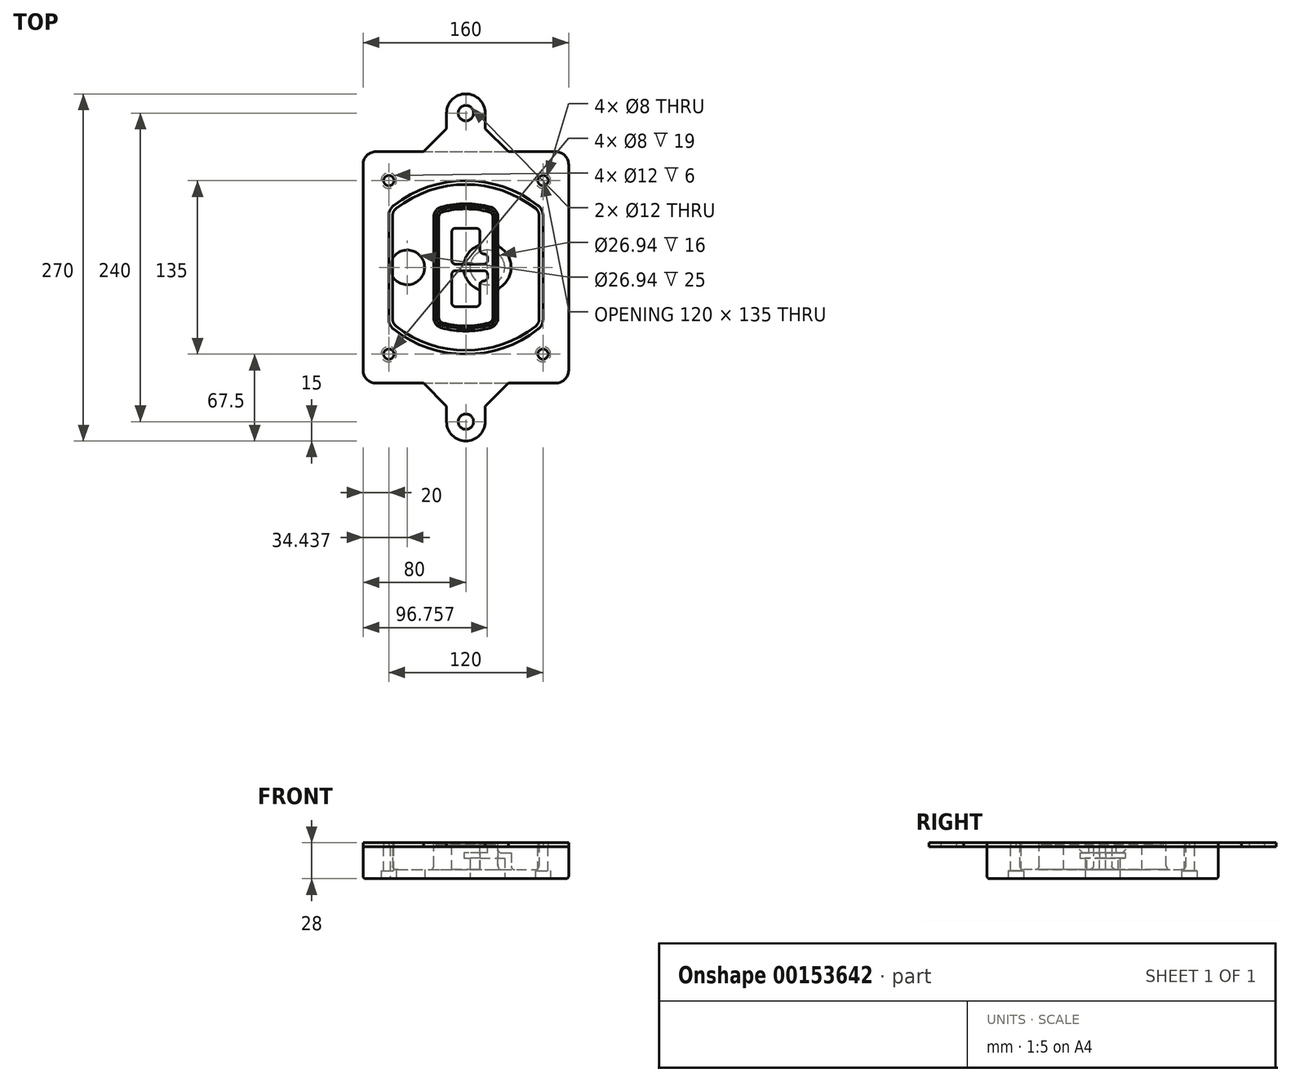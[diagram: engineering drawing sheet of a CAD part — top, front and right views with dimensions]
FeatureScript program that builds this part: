
annotation { "Feature Type Name" : "Feature", "Feature Type Description" : "" }
export const myFeature = defineFeature(function(context is Context, id is Id, definition is map)
    precondition{}
    {
        {
            var Q0;
            Q0=qCreatedBy(makeId("Top.planeOp"),FACE);
            var sketch = newSketch(context, id + "F0", { "sketchPlane" : qUnion([Q0])});
            skPoint(sketch, "E0.rect.middle", {"position": v(0, 0) * mm});
            skLineSegment(sketch, "E1.bottom", {"start": v(-70, -90) * mm, "end": v(70, -90) * mm});
            skLineSegment(sketch, "E1.top", {"start": v(-70, 90) * mm, "end": v(70, 90) * mm});
            skLineSegment(sketch, "E1.left", {"start": v(-80, -80) * mm, "end": v(-80, 80) * mm});
            skLineSegment(sketch, "E1.right", {"start": v(80, -80) * mm, "end": v(80, 80) * mm});
            skLineSegment(sketch, "E2", {"start": v(-80, 90) * mm, "end": v(80, -90) * mm, "construction": true});
            skLineSegment(sketch, "E3", {"start": v(80, 90) * mm, "end": v(-80, -90) * mm, "construction": true});
            skCircle(sketch, "E4", {"center": v(-60, 67.5) * mm, "radius": 4 * mm});
            skCircle(sketch, "E5", {"center": v(60, 67.5) * mm, "radius": 4 * mm});
            skCircle(sketch, "E6", {"center": v(60, -67.5) * mm, "radius": 4 * mm});
            skCircle(sketch, "E7", {"center": v(-60, -67.5) * mm, "radius": 4 * mm});
            skLineSegment(sketch, "E8", {"start": v(-60, 67.5) * mm, "end": v(60, 67.5) * mm, "construction": true});
            skLineSegment(sketch, "E9", {"start": v(60, 67.5) * mm, "end": v(60, -67.5) * mm, "construction": true});
            skLineSegment(sketch, "E10", {"start": v(60, -67.5) * mm, "end": v(-60, -67.5) * mm, "construction": true});
            skLineSegment(sketch, "E11", {"start": v(-60, -67.5) * mm, "end": v(-60, 67.5) * mm, "construction": true});
            skLineSegment(sketch, "E12", {"start": v(-60, 40.3) * mm, "end": v(-60, -40.3) * mm});
            skLineSegment(sketch, "E13", {"start": v(60, 40.3) * mm, "end": v(60, -40.3) * mm});
            skArc(sketch, "E14", {"start": v(56.15, 48.18) * mm, "mid": v(0, 67.5) * mm, "end": v(-56.15, 48.18) * mm});
            skArc(sketch, "E15", {"start": v(-56.15, -48.18) * mm, "mid": v(0, -67.5) * mm, "end": v(56.15, -48.18) * mm});
            skLineSegment(sketch, "E16", {"start": v(-60, 0) * mm, "end": v(60, 0) * mm, "construction": true});
            skPoint(sketch, "E17.visualSharp", {"position": v(-60, -45) * mm});
            skArc(sketch, "E17.filletArc", {"start": v(-60, -40.3) * mm, "mid": v(-58.99, -44.68) * mm, "end": v(-56.15, -48.18) * mm});
            skPoint(sketch, "E18.visualSharp", {"position": v(-60, 45) * mm});
            skArc(sketch, "E18.filletArc", {"start": v(-56.15, 48.18) * mm, "mid": v(-58.99, 44.68) * mm, "end": v(-60, 40.3) * mm});
            skPoint(sketch, "E19.visualSharp", {"position": v(60, 45) * mm});
            skArc(sketch, "E19.filletArc", {"start": v(60, 40.3) * mm, "mid": v(58.99, 44.68) * mm, "end": v(56.15, 48.18) * mm});
            skPoint(sketch, "E20.visualSharp", {"position": v(60, -45) * mm});
            skArc(sketch, "E20.filletArc", {"start": v(56.15, -48.18) * mm, "mid": v(58.99, -44.68) * mm, "end": v(60, -40.3) * mm});
            skPoint(sketch, "E21.visualSharp", {"position": v(-80, 90) * mm});
            skArc(sketch, "E21.filletArc", {"start": v(-70, 90) * mm, "mid": v(-77.07, 87.07) * mm, "end": v(-80, 80) * mm});
            skPoint(sketch, "E22.visualSharp", {"position": v(80, 90) * mm});
            skArc(sketch, "E22.filletArc", {"start": v(80, 80) * mm, "mid": v(77.07, 87.07) * mm, "end": v(70, 90) * mm});
            skPoint(sketch, "E23.visualSharp", {"position": v(80, -90) * mm});
            skArc(sketch, "E23.filletArc", {"start": v(70, -90) * mm, "mid": v(77.07, -87.07) * mm, "end": v(80, -80) * mm});
            skPoint(sketch, "E24.visualSharp", {"position": v(-80, -90) * mm});
            skArc(sketch, "E24.filletArc", {"start": v(-80, -80) * mm, "mid": v(-77.07, -87.07) * mm, "end": v(-70, -90) * mm});
            skArc(sketch, "E25.0", {"start": v(57, 40.3) * mm, "mid": v(56.3, 43.36) * mm, "end": v(54.3, 45.81) * mm});
            skLineSegment(sketch, "E25.1", {"start": v(57, 40.3) * mm, "end": v(57, -40.3) * mm});
            skArc(sketch, "E25.2", {"start": v(54.3, -45.81) * mm, "mid": v(56.3, -43.36) * mm, "end": v(57, -40.3) * mm});
            skArc(sketch, "E25.3", {"start": v(-54.3, -45.81) * mm, "mid": v(0, -64.5) * mm, "end": v(54.3, -45.81) * mm});
            skArc(sketch, "E25.4", {"start": v(-57, -40.3) * mm, "mid": v(-56.3, -43.36) * mm, "end": v(-54.3, -45.81) * mm});
            skArc(sketch, "E25.5", {"start": v(54.3, 45.81) * mm, "mid": v(0, 64.5) * mm, "end": v(-54.3, 45.81) * mm});
            skLineSegment(sketch, "E25.6", {"start": v(-57, 40.3) * mm, "end": v(-57, -40.3) * mm});
            skArc(sketch, "E25.7", {"start": v(-54.3, 45.81) * mm, "mid": v(-56.3, 43.36) * mm, "end": v(-57, 40.3) * mm});
            skArc(sketch, "E26.0", {"start": v(-58.62, 51.33) * mm, "mid": v(-62.58, 46.43) * mm, "end": v(-64, 40.3) * mm});
            skArc(sketch, "E26.1", {"start": v(58.62, 51.33) * mm, "mid": v(0, 71.5) * mm, "end": v(-58.62, 51.33) * mm});
            skArc(sketch, "E26.2", {"start": v(64, 40.3) * mm, "mid": v(62.58, 46.43) * mm, "end": v(58.62, 51.33) * mm});
            skLineSegment(sketch, "E26.3", {"start": v(64, 40.3) * mm, "end": v(64, -40.3) * mm});
            skArc(sketch, "E26.4", {"start": v(58.62, -51.33) * mm, "mid": v(62.58, -46.43) * mm, "end": v(64, -40.3) * mm});
            skLineSegment(sketch, "E26.5", {"start": v(-64, 40.3) * mm, "end": v(-64, -40.3) * mm});
            skArc(sketch, "E26.6", {"start": v(-58.62, -51.33) * mm, "mid": v(0, -71.5) * mm, "end": v(58.62, -51.33) * mm});
            skArc(sketch, "E26.7", {"start": v(-64, -40.3) * mm, "mid": v(-62.58, -46.43) * mm, "end": v(-58.62, -51.33) * mm});
            skSolve(sketch);
        }
        {
            var Q0;
            Q0=makeQuery(id+"F0.imprint","IMPRINT",FACE,{"disambiguationData":[TD([[makeQuery(id+"F0.imprint","IMPRINT",EDGE,{"derivedFrom":sQuery(id+"F0.wireOp",EDGE,"E1.bottom")}),1.0]])]});
            var Q1;
            Q1=makeQuery(id+"F0.imprint","IMPRINT",FACE,{"disambiguationData":[TD([[makeQuery(id+"F0.imprint","IMPRINT",EDGE,{"derivedFrom":sQuery(id+"F0.wireOp",EDGE,"E12")}),1.0]])]});
            var Q2;
            Q2=makeQuery(id+"F0.imprint","IMPRINT",FACE,{"disambiguationData":[TD([[makeQuery(id+"F0.imprint","IMPRINT",EDGE,{"derivedFrom":sQuery(id+"F0.wireOp",EDGE,"E25.0")}),1.0]])]});
            var Q3;
            Q3=makeQuery(id+"F0.imprint","IMPRINT",FACE,{"disambiguationData":[TD([[makeQuery(id+"F0.imprint","IMPRINT",EDGE,{"derivedFrom":sQuery(id+"F0.wireOp",EDGE,"E12")}),-1.0]])]});
            extrude(context, id + "F1", {"entities" : qUnion([Q0, Q1, Q2, Q3]), "oppositeDirection" : true, "depth" : 25 * mm});
        }
        {
            var Q0;
            Q0=makeQuery(id+"F0.imprint","IMPRINT",FACE,{"disambiguationData":[TD([[makeQuery(id+"F0.imprint","IMPRINT",EDGE,{"derivedFrom":sQuery(id+"F0.wireOp",EDGE,"E12")}),1.0]])]});
            extrude(context, id + "F2", {"entities" : qUnion([Q0]), "operationType" : NewBodyOperationType.ADD, "depth" : 3 * mm});
        }
        {
            var Q0;
            Q0=makeQuery(id+"F0.imprint","IMPRINT",FACE,{"disambiguationData":[TD([[makeQuery(id+"F0.imprint","IMPRINT",EDGE,{"derivedFrom":sQuery(id+"F0.wireOp",EDGE,"E25.0")}),1.0]])]});
            extrude(context, id + "F3", {"entities" : qUnion([Q0]), "operationType" : NewBodyOperationType.REMOVE, "oppositeDirection" : true, "depth" : 18 * mm});
        }
        {
            var Q0;
            Q0=makeQuery(id+"F2.opExtrude","CAP_FACE",FACE,{"disambiguationData":[OSD([sQuery(id+"F0.wireOp",EDGE,"E12"),sQuery(id+"F0.wireOp",EDGE,"E13"),sQuery(id+"F0.wireOp",EDGE,"E14"),sQuery(id+"F0.wireOp",EDGE,"E15"),sQuery(id+"F0.wireOp",EDGE,"E17.filletArc"),sQuery(id+"F0.wireOp",EDGE,"E18.filletArc"),sQuery(id+"F0.wireOp",EDGE,"E19.filletArc"),sQuery(id+"F0.wireOp",EDGE,"E20.filletArc"),sQuery(id+"F0.wireOp",EDGE,"E25.0"),sQuery(id+"F0.wireOp",EDGE,"E25.1"),sQuery(id+"F0.wireOp",EDGE,"E25.2"),sQuery(id+"F0.wireOp",EDGE,"E25.3"),sQuery(id+"F0.wireOp",EDGE,"E25.4"),sQuery(id+"F0.wireOp",EDGE,"E25.5"),sQuery(id+"F0.wireOp",EDGE,"E25.6"),sQuery(id+"F0.wireOp",EDGE,"E25.7")])],"isStart":false});
            var sketch = newSketch(context, id + "F4", { "sketchPlane" : qUnion([Q0])});
            skArc(sketch, "E27.0", {"start": v(-19.08, -46.97) * mm, "mid": v(0, -49.5) * mm, "end": v(19.08, -46.97) * mm});
            skArc(sketch, "E28.0", {"start": v(19.08, 46.97) * mm, "mid": v(0, 49.5) * mm, "end": v(-19.08, 46.97) * mm});
            skLineSegment(sketch, "E29", {"start": v(-25, 39.25) * mm, "end": v(-25, -39.25) * mm});
            skLineSegment(sketch, "E30", {"start": v(25, 39.25) * mm, "end": v(25, -39.25) * mm});
            skLineSegment(sketch, "E31", {"start": v(-25, 45.1) * mm, "end": v(25, 45.1) * mm, "construction": true});
            skLineSegment(sketch, "E32", {"start": v(-25, -45.1) * mm, "end": v(25, -45.1) * mm, "construction": true});
            skPoint(sketch, "E33.visualSharp", {"position": v(-25, 45.1) * mm});
            skArc(sketch, "E33.filletArc", {"start": v(-19.08, 46.97) * mm, "mid": v(-23.35, 44.11) * mm, "end": v(-25, 39.25) * mm});
            skPoint(sketch, "E34.visualSharp", {"position": v(25, 45.1) * mm});
            skArc(sketch, "E34.filletArc", {"start": v(25, 39.25) * mm, "mid": v(23.35, 44.11) * mm, "end": v(19.08, 46.97) * mm});
            skPoint(sketch, "E35.visualSharp", {"position": v(25, -45.1) * mm});
            skArc(sketch, "E35.filletArc", {"start": v(19.08, -46.97) * mm, "mid": v(23.35, -44.11) * mm, "end": v(25, -39.25) * mm});
            skPoint(sketch, "E36.visualSharp", {"position": v(-25, -45.1) * mm});
            skArc(sketch, "E36.filletArc", {"start": v(-25, -39.25) * mm, "mid": v(-23.35, -44.11) * mm, "end": v(-19.08, -46.97) * mm});
            skArc(sketch, "E37.0", {"start": v(54.3, 45.81) * mm, "mid": v(0, 64.5) * mm, "end": v(-54.3, 45.81) * mm});
            skArc(sketch, "E37.1", {"start": v(-54.3, 45.81) * mm, "mid": v(-56.3, 43.36) * mm, "end": v(-57, 40.3) * mm});
            skLineSegment(sketch, "E37.2", {"start": v(-57, 40.3) * mm, "end": v(-57, -40.3) * mm});
            skArc(sketch, "E37.3", {"start": v(-57, -40.3) * mm, "mid": v(-56.3, -43.36) * mm, "end": v(-54.3, -45.81) * mm});
            skArc(sketch, "E37.4", {"start": v(-54.3, -45.81) * mm, "mid": v(0, -64.5) * mm, "end": v(54.3, -45.81) * mm});
            skArc(sketch, "E37.5", {"start": v(54.3, -45.81) * mm, "mid": v(56.3, -43.36) * mm, "end": v(57, -40.3) * mm});
            skLineSegment(sketch, "E37.6", {"start": v(57, 40.3) * mm, "end": v(57, -40.3) * mm});
            skArc(sketch, "E37.7", {"start": v(57, 40.3) * mm, "mid": v(56.3, 43.36) * mm, "end": v(54.3, 45.81) * mm});
            skLineSegment(sketch, "E38.0", {"start": v(23, 39.25) * mm, "end": v(23, -39.25) * mm});
            skArc(sketch, "E38.1", {"start": v(18.56, -45.04) * mm, "mid": v(21.76, -42.9) * mm, "end": v(23, -39.25) * mm});
            skArc(sketch, "E38.2", {"start": v(-18.56, -45.04) * mm, "mid": v(0, -47.5) * mm, "end": v(18.56, -45.04) * mm});
            skArc(sketch, "E38.3", {"start": v(-23, -39.25) * mm, "mid": v(-21.76, -42.9) * mm, "end": v(-18.56, -45.04) * mm});
            skLineSegment(sketch, "E38.4", {"start": v(-23, 39.25) * mm, "end": v(-23, -39.25) * mm});
            skArc(sketch, "E38.5", {"start": v(23, 39.25) * mm, "mid": v(21.76, 42.9) * mm, "end": v(18.56, 45.04) * mm});
            skArc(sketch, "E38.6", {"start": v(-18.56, 45.04) * mm, "mid": v(-21.76, 42.9) * mm, "end": v(-23, 39.25) * mm});
            skArc(sketch, "E38.7", {"start": v(18.56, 45.04) * mm, "mid": v(0, 47.5) * mm, "end": v(-18.56, 45.04) * mm});
            skArc(sketch, "E39.0", {"start": v(21, 39.25) * mm, "mid": v(20.18, 41.68) * mm, "end": v(18.04, 43.1) * mm});
            skLineSegment(sketch, "E39.1", {"start": v(21, 39.25) * mm, "end": v(21, -39.25) * mm});
            skArc(sketch, "E39.2", {"start": v(18.04, -43.1) * mm, "mid": v(20.18, -41.68) * mm, "end": v(21, -39.25) * mm});
            skArc(sketch, "E39.3", {"start": v(-18.04, -43.1) * mm, "mid": v(0, -45.5) * mm, "end": v(18.04, -43.1) * mm});
            skArc(sketch, "E39.4", {"start": v(-21, -39.25) * mm, "mid": v(-20.18, -41.68) * mm, "end": v(-18.04, -43.1) * mm});
            skArc(sketch, "E39.5", {"start": v(18.04, 43.1) * mm, "mid": v(0, 45.5) * mm, "end": v(-18.04, 43.1) * mm});
            skLineSegment(sketch, "E39.6", {"start": v(-21, 39.25) * mm, "end": v(-21, -39.25) * mm});
            skArc(sketch, "E39.7", {"start": v(-18.04, 43.1) * mm, "mid": v(-20.18, 41.68) * mm, "end": v(-21, 39.25) * mm});
            skLineSegment(sketch, "E40", {"start": v(-25, 0) * mm, "end": v(25, 0) * mm, "construction": true});
            skLineSegment(sketch, "E41", {"start": v(-11, 5.5) * mm, "end": v(-11, 27.5) * mm});
            skLineSegment(sketch, "E42", {"start": v(-8, 30.5) * mm, "end": v(8, 30.5) * mm});
            skLineSegment(sketch, "E43", {"start": v(11, 27.5) * mm, "end": v(11, 13.5) * mm});
            skLineSegment(sketch, "E44", {"start": v(14, 10.5) * mm, "end": v(14, 10.5) * mm});
            skLineSegment(sketch, "E45", {"start": v(17, 7.5) * mm, "end": v(17, 5.5) * mm});
            skLineSegment(sketch, "E46", {"start": v(14, 2.5) * mm, "end": v(-8, 2.5) * mm});
            skPoint(sketch, "E47.visualSharp", {"position": v(-11, 30.5) * mm});
            skArc(sketch, "E47.filletArc", {"start": v(-8, 30.5) * mm, "mid": v(-10.12, 29.62) * mm, "end": v(-11, 27.5) * mm});
            skPoint(sketch, "E48.visualSharp", {"position": v(11, 30.5) * mm});
            skArc(sketch, "E48.filletArc", {"start": v(11, 27.5) * mm, "mid": v(10.12, 29.62) * mm, "end": v(8, 30.5) * mm});
            skPoint(sketch, "E49.visualSharp", {"position": v(11, 10.5) * mm});
            skArc(sketch, "E49.filletArc", {"start": v(11, 13.5) * mm, "mid": v(11.88, 11.38) * mm, "end": v(14, 10.5) * mm});
            skPoint(sketch, "E50.visualSharp", {"position": v(17, 10.5) * mm});
            skArc(sketch, "E50.filletArc", {"start": v(17, 7.5) * mm, "mid": v(16.12, 9.62) * mm, "end": v(14, 10.5) * mm});
            skPoint(sketch, "E51.visualSharp", {"position": v(17, 2.5) * mm});
            skArc(sketch, "E51.filletArc", {"start": v(14, 2.5) * mm, "mid": v(16.12, 3.38) * mm, "end": v(17, 5.5) * mm});
            skPoint(sketch, "E52.visualSharp", {"position": v(-11, 2.5) * mm});
            skArc(sketch, "E52.filletArc", {"start": v(-11, 5.5) * mm, "mid": v(-10.12, 3.38) * mm, "end": v(-8, 2.5) * mm});
            skLineSegment(sketch, "E53.0.MirrorCS", {"start": v(14, -2.5) * mm, "end": v(-8, -2.5) * mm});
            skArc(sketch, "E54.0.MirrorCS", {"start": v(-11, -5.5) * mm, "mid": v(-10.12, -3.38) * mm, "end": v(-8, -2.5) * mm});
            skLineSegment(sketch, "E55.0.MirrorCS", {"start": v(-11, -5.5) * mm, "end": v(-11, -27.5) * mm});
            skArc(sketch, "E56.0.MirrorCS", {"start": v(-8, -30.5) * mm, "mid": v(-10.12, -29.62) * mm, "end": v(-11, -27.5) * mm});
            skLineSegment(sketch, "E57.0.MirrorCS", {"start": v(-8, -30.5) * mm, "end": v(8, -30.5) * mm});
            skArc(sketch, "E58.0.MirrorCS", {"start": v(11, -27.5) * mm, "mid": v(10.12, -29.62) * mm, "end": v(8, -30.5) * mm});
            skLineSegment(sketch, "E59.0.MirrorCS", {"start": v(11, -27.5) * mm, "end": v(11, -13.5) * mm});
            skArc(sketch, "E60.0.MirrorCS", {"start": v(11, -13.5) * mm, "mid": v(11.88, -11.38) * mm, "end": v(14, -10.5) * mm});
            skArc(sketch, "E61.0.MirrorCS", {"start": v(17, -7.5) * mm, "mid": v(16.12, -9.62) * mm, "end": v(14, -10.5) * mm});
            skLineSegment(sketch, "E62.0.MirrorCS", {"start": v(17, -7.5) * mm, "end": v(17, -5.5) * mm});
            skArc(sketch, "E63.0.MirrorCS", {"start": v(14, -2.5) * mm, "mid": v(16.12, -3.38) * mm, "end": v(17, -5.5) * mm});
            skSolve(sketch);
        }
        {
            var Q0;
            Q0=makeQuery(id+"F4.imprint","IMPRINT",FACE,{"disambiguationData":[TD([[makeQuery(id+"F4.imprint","IMPRINT",EDGE,{"derivedFrom":sQuery(id+"F4.wireOp",EDGE,"E27.0")}),1.0]])]});
            var Q1;
            Q1=makeQuery(id+"F4.imprint","IMPRINT",FACE,{"disambiguationData":[TD([[makeQuery(id+"F4.imprint","IMPRINT",EDGE,{"derivedFrom":sQuery(id+"F4.wireOp",EDGE,"E38.0")}),-1.0]])]});
            var Q2;
            Q2=makeQuery(id+"F4.imprint","IMPRINT",FACE,{"disambiguationData":[TD([[makeQuery(id+"F4.imprint","IMPRINT",EDGE,{"derivedFrom":sQuery(id+"F4.wireOp",EDGE,"E39.0")}),1.0]])]});
            extrude(context, id + "F5", {"entities" : qUnion([Q0, Q1, Q2]), "operationType" : NewBodyOperationType.ADD, "endBound" : BoundingType.UP_TO_NEXT, "oppositeDirection" : true, "depth" : 25 * mm});
        }
        {
            var Q0;
            Q0=makeQuery(id+"F4.imprint","IMPRINT",FACE,{"disambiguationData":[TD([[makeQuery(id+"F4.imprint","IMPRINT",EDGE,{"derivedFrom":sQuery(id+"F4.wireOp",EDGE,"E38.0")}),-1.0]])]});
            extrude(context, id + "F6", {"entities" : qUnion([Q0]), "operationType" : NewBodyOperationType.REMOVE, "oppositeDirection" : true, "depth" : 2 * mm});
        }
        {
            var Q0;
            Q0=makeQuery(id+"F1.opExtrude","CAP_FACE",FACE,{"disambiguationData":[OSD([sQuery(id+"F0.wireOp",EDGE,"E1.bottom"),sQuery(id+"F0.wireOp",EDGE,"E1.top"),sQuery(id+"F0.wireOp",EDGE,"E1.left"),sQuery(id+"F0.wireOp",EDGE,"E1.right"),sQuery(id+"F0.wireOp",EDGE,"E4"),sQuery(id+"F0.wireOp",EDGE,"E5"),sQuery(id+"F0.wireOp",EDGE,"E6"),sQuery(id+"F0.wireOp",EDGE,"E7"),sQuery(id+"F0.wireOp",EDGE,"E21.filletArc"),sQuery(id+"F0.wireOp",EDGE,"E22.filletArc"),sQuery(id+"F0.wireOp",EDGE,"E23.filletArc"),sQuery(id+"F0.wireOp",EDGE,"E24.filletArc")])],"isStart":false});
            var sketch = newSketch(context, id + "F7", { "sketchPlane" : qUnion([Q0])});
            skCircle(sketch, "E64", {"center": v(16.76, 0) * mm, "radius": 13.47 * mm});
            skCircle(sketch, "E65", {"center": v(-45.56, 0) * mm, "radius": 13.47 * mm});
            skLineSegment(sketch, "E66", {"start": v(80, 0) * mm, "end": v(-80, 0) * mm});
            skCircle(sketch, "E67", {"center": v(16.76, 0) * mm, "radius": 18.47 * mm});
            skCircle(sketch, "E68", {"center": v(60, -67.5) * mm, "radius": 6 * mm});
            skCircle(sketch, "E69", {"center": v(-60, -67.5) * mm, "radius": 6 * mm});
            skCircle(sketch, "E70", {"center": v(-60, 67.5) * mm, "radius": 6 * mm});
            skCircle(sketch, "E71", {"center": v(60, 67.5) * mm, "radius": 6 * mm});
            skSolve(sketch);
        }
        {
            var Q0;
            {var subQ1=sQuery(id+"F7.wireOp",EDGE,"E66");var subQ4=sQuery(id+"F7.wireOp",EDGE,"E64");var subQ6=makeQuery(id+"F7.imprint","INTERSECT",VERTEX,{"disambiguationData":[OD(0.0)],"derivedFrom":[subQ4,subQ1]});Q0=makeQuery(id+"F7.imprint","IMPRINT",FACE,{"disambiguationData":[TD([[makeQuery(id+"F7.imprint","IMPRINT",EDGE,{"disambiguationData":[TD([[subQ6,-1.0]])],"derivedFrom":subQ4}),-1.0]])]});}
            var Q1;
            {var subQ0=sQuery(id+"F7.wireOp",EDGE,"E66");var subQ1=sQuery(id+"F7.wireOp",EDGE,"E64");var subQ3=makeQuery(id+"F7.imprint","INTERSECT",VERTEX,{"disambiguationData":[OD(0.0)],"derivedFrom":[subQ1,subQ0]});Q1=makeQuery(id+"F7.imprint","IMPRINT",FACE,{"disambiguationData":[TD([[makeQuery(id+"F7.imprint","IMPRINT",EDGE,{"disambiguationData":[TD([[subQ3,-1.0]])],"derivedFrom":subQ1}),1.0]])]});}
            var Q2;
            {var subQ0=sQuery(id+"F7.wireOp",EDGE,"E66");var subQ1=sQuery(id+"F7.wireOp",EDGE,"E64");var subQ3=makeQuery(id+"F7.imprint","INTERSECT",VERTEX,{"disambiguationData":[OD(0.0)],"derivedFrom":[subQ1,subQ0]});Q2=makeQuery(id+"F7.imprint","IMPRINT",FACE,{"disambiguationData":[TD([[makeQuery(id+"F7.imprint","IMPRINT",EDGE,{"disambiguationData":[TD([[subQ3,1.0]])],"derivedFrom":subQ1}),1.0]])]});}
            var Q3;
            {var subQ1=sQuery(id+"F7.wireOp",EDGE,"E66");var subQ4=sQuery(id+"F7.wireOp",EDGE,"E64");var subQ6=makeQuery(id+"F7.imprint","INTERSECT",VERTEX,{"disambiguationData":[OD(0.0)],"derivedFrom":[subQ4,subQ1]});Q3=makeQuery(id+"F7.imprint","IMPRINT",FACE,{"disambiguationData":[TD([[makeQuery(id+"F7.imprint","IMPRINT",EDGE,{"disambiguationData":[TD([[subQ6,1.0]])],"derivedFrom":subQ4}),-1.0]])]});}
            extrude(context, id + "F8", {"entities" : qUnion([Q0, Q1, Q2, Q3]), "operationType" : NewBodyOperationType.ADD, "oppositeDirection" : true, "depth" : 20 * mm});
        }
        {
            var Q0;
            {var subQ0=sQuery(id+"F7.wireOp",EDGE,"E66");var subQ1=sQuery(id+"F7.wireOp",EDGE,"E64");var subQ3=makeQuery(id+"F7.imprint","INTERSECT",VERTEX,{"disambiguationData":[OD(0.0)],"derivedFrom":[subQ1,subQ0]});Q0=makeQuery(id+"F7.imprint","IMPRINT",FACE,{"disambiguationData":[TD([[makeQuery(id+"F7.imprint","IMPRINT",EDGE,{"disambiguationData":[TD([[subQ3,-1.0]])],"derivedFrom":subQ1}),1.0]])]});}
            var Q1;
            {var subQ0=sQuery(id+"F7.wireOp",EDGE,"E66");var subQ1=sQuery(id+"F7.wireOp",EDGE,"E64");var subQ3=makeQuery(id+"F7.imprint","INTERSECT",VERTEX,{"disambiguationData":[OD(0.0)],"derivedFrom":[subQ1,subQ0]});Q1=makeQuery(id+"F7.imprint","IMPRINT",FACE,{"disambiguationData":[TD([[makeQuery(id+"F7.imprint","IMPRINT",EDGE,{"disambiguationData":[TD([[subQ3,1.0]])],"derivedFrom":subQ1}),1.0]])]});}
            extrude(context, id + "F9", {"entities" : qUnion([Q0, Q1]), "operationType" : NewBodyOperationType.REMOVE, "oppositeDirection" : true, "depth" : 16 * mm});
        }
        {
            var Q0;
            {var subQ0=sQuery(id+"F7.wireOp",EDGE,"E66");var subQ1=sQuery(id+"F7.wireOp",EDGE,"E65");var subQ3=makeQuery(id+"F7.imprint","INTERSECT",VERTEX,{"disambiguationData":[OD(0.0)],"derivedFrom":[subQ1,subQ0]});Q0=makeQuery(id+"F7.imprint","IMPRINT",FACE,{"disambiguationData":[TD([[makeQuery(id+"F7.imprint","IMPRINT",EDGE,{"disambiguationData":[TD([[subQ3,-1.0]])],"derivedFrom":subQ1}),1.0]])]});}
            var Q1;
            {var subQ0=sQuery(id+"F7.wireOp",EDGE,"E66");var subQ1=sQuery(id+"F7.wireOp",EDGE,"E65");var subQ3=makeQuery(id+"F7.imprint","INTERSECT",VERTEX,{"disambiguationData":[OD(0.0)],"derivedFrom":[subQ1,subQ0]});Q1=makeQuery(id+"F7.imprint","IMPRINT",FACE,{"disambiguationData":[TD([[makeQuery(id+"F7.imprint","IMPRINT",EDGE,{"disambiguationData":[TD([[subQ3,1.0]])],"derivedFrom":subQ1}),1.0]])]});}
            extrude(context, id + "F10", {"entities" : qUnion([Q0, Q1]), "operationType" : NewBodyOperationType.REMOVE, "oppositeDirection" : true, "depth" : 25 * mm});
        }
        {
            var Q0;
            Q0=makeQuery(id+"F7.imprint","IMPRINT",FACE,{"disambiguationData":[TD([[makeQuery(id+"F7.imprint","IMPRINT",EDGE,{"derivedFrom":sQuery(id+"F7.wireOp",EDGE,"E68")}),1.0]])]});
            var Q1;
            Q1=makeQuery(id+"F7.imprint","IMPRINT",FACE,{"disambiguationData":[TD([[makeQuery(id+"F7.imprint","IMPRINT",EDGE,{"derivedFrom":makeQuery(id+"F1.opExtrude","CAP_EDGE",EDGE,{"disambiguationData":[OSD([sQuery(id+"F0.wireOp",EDGE,"E5")])],"isStart":false})}),-1.0]])]});
            var Q2;
            Q2=makeQuery(id+"F7.imprint","IMPRINT",FACE,{"disambiguationData":[TD([[makeQuery(id+"F7.imprint","IMPRINT",EDGE,{"derivedFrom":sQuery(id+"F7.wireOp",EDGE,"E69")}),1.0]])]});
            var Q3;
            Q3=makeQuery(id+"F7.imprint","IMPRINT",FACE,{"disambiguationData":[TD([[makeQuery(id+"F7.imprint","IMPRINT",EDGE,{"derivedFrom":makeQuery(id+"F1.opExtrude","CAP_EDGE",EDGE,{"disambiguationData":[OSD([sQuery(id+"F0.wireOp",EDGE,"E4")])],"isStart":false})}),-1.0]])]});
            var Q4;
            Q4=makeQuery(id+"F7.imprint","IMPRINT",FACE,{"disambiguationData":[TD([[makeQuery(id+"F7.imprint","IMPRINT",EDGE,{"derivedFrom":sQuery(id+"F7.wireOp",EDGE,"E70")}),1.0]])]});
            var Q5;
            Q5=makeQuery(id+"F7.imprint","IMPRINT",FACE,{"disambiguationData":[TD([[makeQuery(id+"F7.imprint","IMPRINT",EDGE,{"derivedFrom":makeQuery(id+"F1.opExtrude","CAP_EDGE",EDGE,{"disambiguationData":[OSD([sQuery(id+"F0.wireOp",EDGE,"E7")])],"isStart":false})}),-1.0]])]});
            var Q6;
            Q6=makeQuery(id+"F7.imprint","IMPRINT",FACE,{"disambiguationData":[TD([[makeQuery(id+"F7.imprint","IMPRINT",EDGE,{"derivedFrom":sQuery(id+"F7.wireOp",EDGE,"E71")}),1.0]])]});
            var Q7;
            Q7=makeQuery(id+"F7.imprint","IMPRINT",FACE,{"disambiguationData":[TD([[makeQuery(id+"F7.imprint","IMPRINT",EDGE,{"derivedFrom":makeQuery(id+"F1.opExtrude","CAP_EDGE",EDGE,{"disambiguationData":[OSD([sQuery(id+"F0.wireOp",EDGE,"E6")])],"isStart":false})}),-1.0]])]});
            extrude(context, id + "F11", {"entities" : qUnion([Q0, Q1, Q2, Q3, Q4, Q5, Q6, Q7]), "operationType" : NewBodyOperationType.REMOVE, "oppositeDirection" : true, "depth" : 6 * mm});
        }
        {
            var Q0;
            Q0=makeQuery(id+"F9.boolean.opBoolean","COPY",FACE,{"derivedFrom":makeQuery(id+"F9.opExtrude","CAP_FACE",FACE,{"disambiguationData":[OSD([sQuery(id+"F7.wireOp",EDGE,"E64")])],"isStart":false})});
            var sketch = newSketch(context, id + "F12", { "sketchPlane" : qUnion([Q0])});
            skArc(sketch, "E72.0", {"start": v(11, 17.55) * mm, "mid": v(2.57, 11.82) * mm, "end": v(-1.54, 2.5) * mm});
            skArc(sketch, "E72.1", {"start": v(-1.54, -2.5) * mm, "mid": v(2.57, -11.82) * mm, "end": v(11, -17.55) * mm});
            skLineSegment(sketch, "E73", {"start": v(-1.54, -2.5) * mm, "end": v(14, -2.5) * mm});
            skLineSegment(sketch, "E74.0", {"start": v(14, 2.5) * mm, "end": v(-1.54, 2.5) * mm});
            skArc(sketch, "E74.1", {"start": v(14, 2.5) * mm, "mid": v(16.12, 3.38) * mm, "end": v(17, 5.5) * mm});
            skLineSegment(sketch, "E74.2", {"start": v(17, 7.5) * mm, "end": v(17, 5.5) * mm});
            skArc(sketch, "E74.3", {"start": v(17, 7.5) * mm, "mid": v(16.12, 9.62) * mm, "end": v(14, 10.5) * mm});
            skArc(sketch, "E74.4", {"start": v(11, 13.5) * mm, "mid": v(11.88, 11.38) * mm, "end": v(14, 10.5) * mm});
            skLineSegment(sketch, "E74.5", {"start": v(11, 17.55) * mm, "end": v(11, 13.5) * mm});
            skLineSegment(sketch, "E74.7", {"start": v(14, -2.5) * mm, "end": v(-1.54, -2.5) * mm});
            skArc(sketch, "E74.8", {"start": v(14, -2.5) * mm, "mid": v(16.12, -3.38) * mm, "end": v(17, -5.5) * mm});
            skLineSegment(sketch, "E74.9", {"start": v(17, -7.5) * mm, "end": v(17, -5.5) * mm});
            skArc(sketch, "E74.10", {"start": v(17, -7.5) * mm, "mid": v(16.12, -9.62) * mm, "end": v(14, -10.5) * mm});
            skArc(sketch, "E74.11", {"start": v(11, -13.5) * mm, "mid": v(11.88, -11.38) * mm, "end": v(14, -10.5) * mm});
            skLineSegment(sketch, "E74.12", {"start": v(11, -17.55) * mm, "end": v(11, -13.5) * mm});
            skPoint(sketch, "E75.orphan", {"position": v(11, -27.5) * mm});
            skPoint(sketch, "E76.orphan", {"position": v(-8, -2.5) * mm});
            skPoint(sketch, "E77.orphan", {"position": v(-8, 2.5) * mm});
            skPoint(sketch, "E78.orphan", {"position": v(11, 27.5) * mm});
            skSolve(sketch);
        }
        {
            var Q0;
            {var subQ7=sQuery(id+"F12.wireOp",EDGE,"E72.0");var subQ14=sQuery(id+"F12.wireOp",EDGE,"E72.1");var subQ16=sQuery(id+"F12.wireOp",EDGE,"E74.1");var subQ18=sQuery(id+"F12.wireOp",EDGE,"E74.8");Q0=qUnion([makeQuery(id+"F12.imprint","IMPRINT",FACE,{"disambiguationData":[TD([[makeQuery(id+"F12.imprint","IMPRINT",EDGE,{"derivedFrom":subQ7}),1.0]])]}),makeQuery(id+"F12.imprint","IMPRINT",FACE,{"disambiguationData":[TD([[makeQuery(id+"F12.imprint","IMPRINT",EDGE,{"derivedFrom":subQ14}),1.0]])]}),makeQuery(id+"F12.imprint","IMPRINT",FACE,{"disambiguationData":[TD([[makeQuery(id+"F12.imprint","IMPRINT",EDGE,{"derivedFrom":subQ16}),1.0]])]}),makeQuery(id+"F12.imprint","IMPRINT",FACE,{"disambiguationData":[TD([[makeQuery(id+"F12.imprint","IMPRINT",EDGE,{"derivedFrom":subQ18}),-1.0]])]})]);}
            var Q1;
            Q1=makeQuery(id+"F5.boolean.opBoolean","SPLIT",FACE,{"disambiguationData":[TD([makeQuery(id+"F5.opExtrude","SWEPT_FACE",FACE,{"disambiguationData":[OSD([sQuery(id+"F4.wireOp",EDGE,"E41")])]})])],"derivedFrom":makeQuery(id+"F3.boolean.opBoolean","COPY",FACE,{"derivedFrom":makeQuery(id+"F3.opExtrude","CAP_FACE",FACE,{"disambiguationData":[OSD([sQuery(id+"F0.wireOp",EDGE,"E25.0"),sQuery(id+"F0.wireOp",EDGE,"E25.1"),sQuery(id+"F0.wireOp",EDGE,"E25.2"),sQuery(id+"F0.wireOp",EDGE,"E25.3"),sQuery(id+"F0.wireOp",EDGE,"E25.4"),sQuery(id+"F0.wireOp",EDGE,"E25.5"),sQuery(id+"F0.wireOp",EDGE,"E25.6"),sQuery(id+"F0.wireOp",EDGE,"E25.7")])],"isStart":false})})});
            extrude(context, id + "F13", {"entities" : qUnion([Q0]), "operationType" : NewBodyOperationType.REMOVE, "endBound" : BoundingType.UP_TO_SURFACE, "endBoundEntityFace" : qUnion([Q1]), "depth" : 25 * mm});
        }
        {
            var Q0;
            Q0=makeQuery(id+"F3.boolean.opBoolean","COPY",EDGE,{"derivedFrom":makeQuery(id+"F3.opExtrude","CAP_EDGE",EDGE,{"disambiguationData":[OSD([sQuery(id+"F0.wireOp",EDGE,"E25.6")])],"isStart":false})});
            var Q1;
            Q1=makeQuery(id+"F8.boolean.opBoolean","INTERSECT",EDGE,{"derivedFrom":[makeQuery(id+"F5.opExtrude","SWEPT_FACE",FACE,{"disambiguationData":[OSD([sQuery(id+"F4.wireOp",EDGE,"E30")])]}),makeQuery(id+"F8.opExtrude","CAP_FACE",FACE,{"disambiguationData":[OSD([sQuery(id+"F7.wireOp",EDGE,"E67")])],"isStart":false})]});
            var Q2;
            Q2=makeQuery(id+"F8.boolean.opBoolean","INTERSECT",EDGE,{"disambiguationData":[OD(1.0)],"derivedFrom":[makeQuery(id+"F5.opExtrude","SWEPT_FACE",FACE,{"disambiguationData":[OSD([sQuery(id+"F4.wireOp",EDGE,"E30")])]}),makeQuery(id+"F8.opExtrude","SWEPT_FACE",FACE,{"disambiguationData":[OSD([sQuery(id+"F7.wireOp",EDGE,"E67")])]})]});
            var Q3;
            {var subQ0=sQuery(id+"F4.wireOp",EDGE,"E30");Q3=makeQuery(id+"F8.boolean.opBoolean","SPLIT",EDGE,{"disambiguationData":[TD([makeQuery(id+"F5.opExtrude","SWEPT_FACE",FACE,{"disambiguationData":[OSD([sQuery(id+"F4.wireOp",EDGE,"E35.filletArc")])]})])],"derivedFrom":makeQuery(id+"F5.opExtrude","CAP_EDGE",EDGE,{"disambiguationData":[OSD([subQ0])],"isStart":false})});}
            var Q4;
            {var subQ0=sQuery(id+"F0.wireOp",EDGE,"E25.7");var subQ1=sQuery(id+"F0.wireOp",EDGE,"E25.1");var subQ2=sQuery(id+"F0.wireOp",EDGE,"E25.6");var subQ3=sQuery(id+"F0.wireOp",EDGE,"E25.5");var subQ4=sQuery(id+"F0.wireOp",EDGE,"E25.4");var subQ5=sQuery(id+"F0.wireOp",EDGE,"E25.0");var subQ6=sQuery(id+"F0.wireOp",EDGE,"E25.2");var subQ7=sQuery(id+"F0.wireOp",EDGE,"E25.3");Q4=makeQuery(id+"F8.boolean.opBoolean","INTERSECT",EDGE,{"derivedFrom":[makeQuery(id+"F5.boolean.opBoolean","SPLIT",FACE,{"disambiguationData":[TD([makeQuery(id+"F2.opExtrude","SWEPT_FACE",FACE,{"disambiguationData":[OSD([subQ5])]})])],"derivedFrom":makeQuery(id+"F3.boolean.opBoolean","COPY",FACE,{"derivedFrom":makeQuery(id+"F3.opExtrude","CAP_FACE",FACE,{"disambiguationData":[OSD([subQ5,subQ1,subQ6,subQ7,subQ4,subQ3,subQ2,subQ0])],"isStart":false})})}),makeQuery(id+"F8.opExtrude","SWEPT_FACE",FACE,{"disambiguationData":[OSD([sQuery(id+"F7.wireOp",EDGE,"E67")])]})]});}
            var Q5;
            Q5=makeQuery(id+"F8.boolean.opBoolean","INTERSECT",EDGE,{"disambiguationData":[OD(0.0)],"derivedFrom":[makeQuery(id+"F5.opExtrude","SWEPT_FACE",FACE,{"disambiguationData":[OSD([sQuery(id+"F4.wireOp",EDGE,"E30")])]}),makeQuery(id+"F8.opExtrude","SWEPT_FACE",FACE,{"disambiguationData":[OSD([sQuery(id+"F7.wireOp",EDGE,"E67")])]})]});
            fillet(context, id + "F14", {"entities" : qUnion([Q0, Q1, Q2, Q3, Q4, Q5]), "radius" : 3 * mm, "tangentPropagation" : true, "allowEdgeOverflow" : false});
        }
        {
            var Q0;
            Q0=makeQuery(id+"F1.opExtrude","CAP_EDGE",EDGE,{"disambiguationData":[OSD([sQuery(id+"F0.wireOp",EDGE,"E1.bottom")])],"isStart":false});
            fillet(context, id + "F15", {"entities" : qUnion([Q0]), "radius" : 2 * mm, "tangentPropagation" : true, "allowEdgeOverflow" : false});
        }
        {
            var Q0;
            {var subQ0=sQuery(id+"F0.wireOp",EDGE,"E22.filletArc");var subQ1=sQuery(id+"F0.wireOp",EDGE,"E7");var subQ2=sQuery(id+"F0.wireOp",EDGE,"E6");var subQ3=sQuery(id+"F0.wireOp",EDGE,"E5");var subQ4=sQuery(id+"F0.wireOp",EDGE,"E4");var subQ5=sQuery(id+"F0.wireOp",EDGE,"E1.bottom");var subQ6=sQuery(id+"F0.wireOp",EDGE,"E21.filletArc");var subQ7=sQuery(id+"F0.wireOp",EDGE,"E1.top");var subQ8=sQuery(id+"F0.wireOp",EDGE,"E1.left");var subQ9=sQuery(id+"F0.wireOp",EDGE,"E1.right");var subQ10=sQuery(id+"F0.wireOp",EDGE,"E23.filletArc");var subQ11=sQuery(id+"F0.wireOp",EDGE,"E24.filletArc");Q0=makeQuery(id+"F2.boolean.opBoolean","SPLIT",FACE,{"disambiguationData":[TD([makeQuery(id+"F1.opExtrude","SWEPT_FACE",FACE,{"disambiguationData":[OSD([subQ5])]})])],"derivedFrom":makeQuery(id+"F1.opExtrude","CAP_FACE",FACE,{"disambiguationData":[OSD([subQ5,subQ7,subQ8,subQ9,subQ4,subQ3,subQ2,subQ1,subQ6,subQ0,subQ10,subQ11])],"isStart":true})});}
            var sketch = newSketch(context, id + "F16", { "sketchPlane" : qUnion([Q0])});
            skLineSegment(sketch, "E79.0", {"start": v(-70, 90) * mm, "end": v(70, 90) * mm});
            skArc(sketch, "E79.1", {"start": v(80, 80) * mm, "mid": v(77.07, 87.07) * mm, "end": v(70, 90) * mm});
            skLineSegment(sketch, "E79.2", {"start": v(80, -80) * mm, "end": v(80, 80) * mm});
            skArc(sketch, "E79.3", {"start": v(70, -90) * mm, "mid": v(77.07, -87.07) * mm, "end": v(80, -80) * mm});
            skLineSegment(sketch, "E79.4", {"start": v(-70, -90) * mm, "end": v(70, -90) * mm});
            skArc(sketch, "E79.5", {"start": v(-80, -80) * mm, "mid": v(-77.07, -87.07) * mm, "end": v(-70, -90) * mm});
            skLineSegment(sketch, "E79.6", {"start": v(-80, -80) * mm, "end": v(-80, 80) * mm});
            skLineSegment(sketch, "E79.7", {"start": v(-60, 40.3) * mm, "end": v(-60, -40.3) * mm});
            skArc(sketch, "E79.8", {"start": v(-60, -40.3) * mm, "mid": v(-58.99, -44.68) * mm, "end": v(-56.15, -48.18) * mm});
            skArc(sketch, "E79.9", {"start": v(-56.15, -48.18) * mm, "mid": v(0, -67.5) * mm, "end": v(56.15, -48.18) * mm});
            skArc(sketch, "E79.10", {"start": v(56.15, -48.18) * mm, "mid": v(58.99, -44.68) * mm, "end": v(60, -40.3) * mm});
            skLineSegment(sketch, "E79.11", {"start": v(60, 40.3) * mm, "end": v(60, -40.3) * mm});
            skArc(sketch, "E79.12", {"start": v(60, 40.3) * mm, "mid": v(58.99, 44.68) * mm, "end": v(56.15, 48.18) * mm});
            skArc(sketch, "E79.13", {"start": v(56.15, 48.18) * mm, "mid": v(0, 67.5) * mm, "end": v(-56.15, 48.18) * mm});
            skArc(sketch, "E79.14", {"start": v(-56.15, 48.18) * mm, "mid": v(-58.99, 44.68) * mm, "end": v(-60, 40.3) * mm});
            skArc(sketch, "E79.15", {"start": v(-70, 90) * mm, "mid": v(-77.07, 87.07) * mm, "end": v(-80, 80) * mm});
            skCircle(sketch, "E79.16", {"center": v(-60, 67.5) * mm, "radius": 4 * mm});
            skCircle(sketch, "E79.17", {"center": v(60, 67.5) * mm, "radius": 4 * mm});
            skCircle(sketch, "E79.18", {"center": v(60, -67.5) * mm, "radius": 4 * mm});
            skCircle(sketch, "E79.19", {"center": v(-60, -67.5) * mm, "radius": 4 * mm});
            skLineSegment(sketch, "E80", {"start": v(0, 90) * mm, "end": v(0, 120) * mm, "construction": true});
            skCircle(sketch, "E81", {"center": v(0, 120) * mm, "radius": 6 * mm});
            skArc(sketch, "E82", {"start": v(15, 120) * mm, "mid": v(0, 135) * mm, "end": v(-15, 120) * mm});
            skLineSegment(sketch, "E83", {"start": v(-15, 120) * mm, "end": v(-15, 108) * mm});
            skLineSegment(sketch, "E84", {"start": v(-15, 108) * mm, "end": v(-33, 90) * mm});
            skLineSegment(sketch, "E85", {"start": v(15, 120) * mm, "end": v(15, 108) * mm});
            skLineSegment(sketch, "E86", {"start": v(15, 108) * mm, "end": v(33, 90) * mm});
            skLineSegment(sketch, "E87", {"start": v(-80, 0) * mm, "end": v(80, 0) * mm, "construction": true});
            skLineSegment(sketch, "E88.MirrorCS", {"start": v(0, -90) * mm, "end": v(0, -120) * mm, "construction": true});
            skLineSegment(sketch, "E89.MirrorCS", {"start": v(15, -108) * mm, "end": v(33, -90) * mm});
            skLineSegment(sketch, "E90.MirrorCS", {"start": v(-15, -108) * mm, "end": v(-33, -90) * mm});
            skArc(sketch, "E91.MirrorCS", {"start": v(15, -120) * mm, "mid": v(0, -135) * mm, "end": v(-15, -120) * mm});
            skLineSegment(sketch, "E92.MirrorCS", {"start": v(-15, -120) * mm, "end": v(-15, -108) * mm});
            skCircle(sketch, "E93.MirrorC", {"center": v(0, -120) * mm, "radius": 6 * mm});
            skLineSegment(sketch, "E94.MirrorCS", {"start": v(15, -120) * mm, "end": v(15, -108) * mm});
            skSolve(sketch);
        }
        {
            var Q0;
            Q0 = qSketchRegion(id + "F16", true);
            var Q1;
            Q1=makeQuery(id+"F2.opExtrude","CAP_FACE",FACE,{"disambiguationData":[OSD([sQuery(id+"F0.wireOp",EDGE,"E12"),sQuery(id+"F0.wireOp",EDGE,"E13"),sQuery(id+"F0.wireOp",EDGE,"E14"),sQuery(id+"F0.wireOp",EDGE,"E15"),sQuery(id+"F0.wireOp",EDGE,"E17.filletArc"),sQuery(id+"F0.wireOp",EDGE,"E18.filletArc"),sQuery(id+"F0.wireOp",EDGE,"E19.filletArc"),sQuery(id+"F0.wireOp",EDGE,"E20.filletArc"),sQuery(id+"F0.wireOp",EDGE,"E25.0"),sQuery(id+"F0.wireOp",EDGE,"E25.1"),sQuery(id+"F0.wireOp",EDGE,"E25.2"),sQuery(id+"F0.wireOp",EDGE,"E25.3"),sQuery(id+"F0.wireOp",EDGE,"E25.4"),sQuery(id+"F0.wireOp",EDGE,"E25.5"),sQuery(id+"F0.wireOp",EDGE,"E25.6"),sQuery(id+"F0.wireOp",EDGE,"E25.7")])],"isStart":false});
            var Q2;
            Q2=makeQuery(id+"F1.opExtrude","SWEPT_BODY",BODY,{"disambiguationData":[OSD([sQuery(id+"F0.wireOp",EDGE,"E1.bottom"),sQuery(id+"F0.wireOp",EDGE,"E1.top"),sQuery(id+"F0.wireOp",EDGE,"E1.left"),sQuery(id+"F0.wireOp",EDGE,"E1.right"),sQuery(id+"F0.wireOp",EDGE,"E4"),sQuery(id+"F0.wireOp",EDGE,"E5"),sQuery(id+"F0.wireOp",EDGE,"E6"),sQuery(id+"F0.wireOp",EDGE,"E7"),sQuery(id+"F0.wireOp",EDGE,"E21.filletArc"),sQuery(id+"F0.wireOp",EDGE,"E22.filletArc"),sQuery(id+"F0.wireOp",EDGE,"E23.filletArc"),sQuery(id+"F0.wireOp",EDGE,"E24.filletArc")])]});
            extrude(context, id + "F17", {"entities" : qUnion([Q0]), "endBound" : BoundingType.UP_TO_SURFACE, "endBoundEntityFace" : qUnion([Q1]), "endBoundEntityBody" : qUnion([Q2]), "depth" : 25 * mm});
        }
    });
